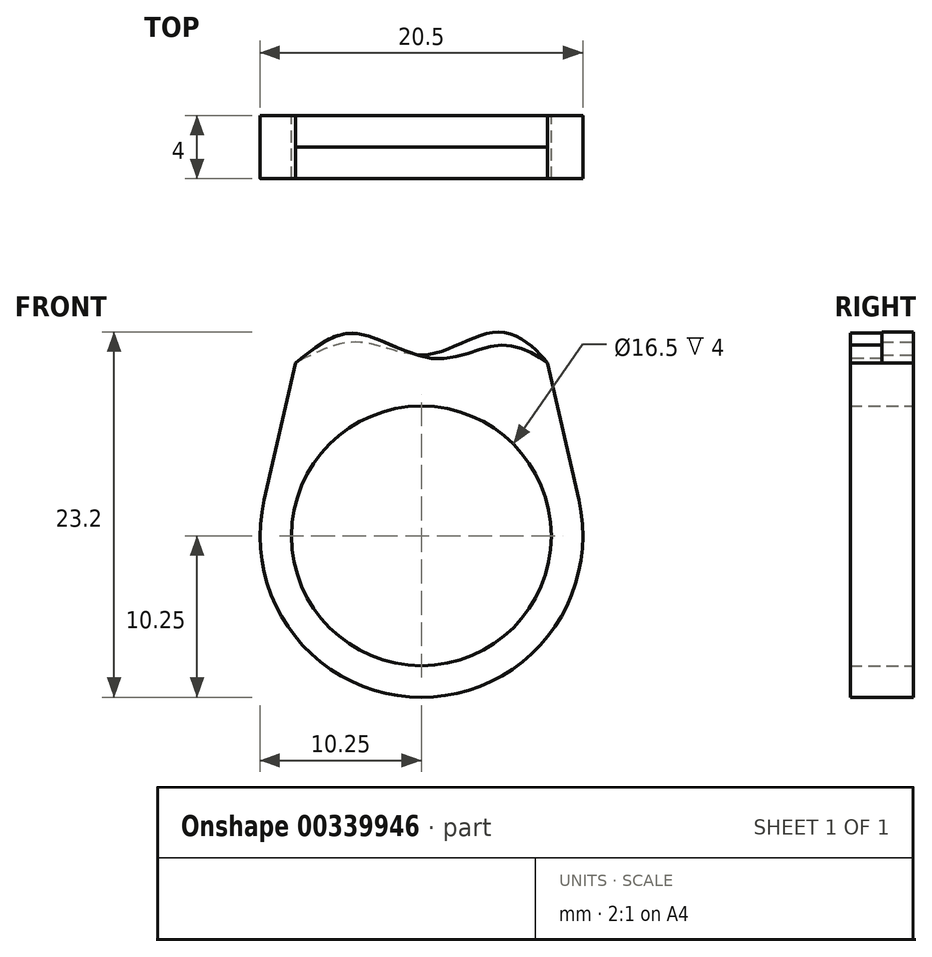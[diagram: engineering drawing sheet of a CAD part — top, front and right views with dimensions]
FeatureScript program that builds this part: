
annotation { "Feature Type Name" : "Feature", "Feature Type Description" : "" }
export const myFeature = defineFeature(function(context is Context, id is Id, definition is map)
    precondition{}
    {
        {
            var Q0;
            Q0=qCreatedBy(makeId("Front.planeOp"),FACE);
            var sketch = newSketch(context, id + "F0", { "sketchPlane" : qUnion([Q0])});
            skCircle(sketch, "E0", {"center": v(0, 0) * mm, "radius": 8.25 * mm});
            skCircle(sketch, "E1", {"center": v(0, 0) * mm, "radius": 10.25 * mm});
            skLineSegment(sketch, "E2", {"start": v(-10, 2.28) * mm, "end": v(-8, 11) * mm});
            skLineSegment(sketch, "E3", {"start": v(-8, 11) * mm, "end": v(8, 11) * mm});
            skLineSegment(sketch, "E4", {"start": v(8, 11) * mm, "end": v(10, 2.28) * mm});
            skLineSegment(sketch, "E5", {"start": v(0, 11) * mm, "end": v(0, 0) * mm});
            skSolve(sketch);
        }
        {
            var Q0;
            Q0 = qSketchRegion(id + "F0", true);
            extrude(context, id + "F1", {"entities" : qUnion([Q0]), "depth" : 2 * mm, "hasSecondDirection" : true, "secondDirectionOppositeDirection" : true, "secondDirectionDepth" : 2 * mm});
        }
        {
            var Q0;
            Q0=makeQuery(id+"F1.opExtrude","CAP_FACE",FACE,{"disambiguationData":[OSD([sQuery(id+"F0.wireOp",EDGE,"E0"),sQuery(id+"F0.wireOp",EDGE,"E1"),sQuery(id+"F0.wireOp",EDGE,"E2"),sQuery(id+"F0.wireOp",EDGE,"E3"),sQuery(id+"F0.wireOp",EDGE,"E4")])],"isStart":false});
            var sketch = newSketch(context, id + "F2", { "sketchPlane" : qUnion([Q0])});
            skFitSpline(sketch, "E6", {"points": [v(-8, 11) * mm, v(-4.31, 12.87) * mm, v(0.78, 11.26) * mm, v(5.12, 12.12) * mm, v(8, 11) * mm], "startDerivative": vector(15.2, 11.43) * mm, "endDerivative": vector(10.8, -7.66) * mm});
            skLineSegment(sketch, "E7", {"start": v(-8, 11) * mm, "end": v(8, 11) * mm});
            skSolve(sketch);
        }
        {
            var Q0;
            Q0 = qSketchRegion(id + "F2", true);
            extrude(context, id + "F3", {"entities" : qUnion([Q0]), "operationType" : NewBodyOperationType.ADD, "oppositeDirection" : true, "depth" : 2 * mm});
        }
        {
            var Q0;
            Q0=makeQuery(id+"F1.opExtrude","CAP_FACE",FACE,{"disambiguationData":[OSD([sQuery(id+"F0.wireOp",EDGE,"E0"),sQuery(id+"F0.wireOp",EDGE,"E1"),sQuery(id+"F0.wireOp",EDGE,"E2"),sQuery(id+"F0.wireOp",EDGE,"E3"),sQuery(id+"F0.wireOp",EDGE,"E4")])],"isStart":true});
            var sketch = newSketch(context, id + "F4", { "sketchPlane" : qUnion([Q0])});
            skFitSpline(sketch, "E8", {"points": [v(-8, 11) * mm, v(-4.96, 12.95) * mm, v(-0.34, 11.51) * mm, v(4.16, 12.31) * mm, v(8, 11) * mm], "startDerivative": vector(8.84, 10.98) * mm, "endDerivative": vector(14.38, -6.84) * mm});
            skLineSegment(sketch, "E9", {"start": v(-8, 11) * mm, "end": v(8, 11) * mm});
            skSolve(sketch);
        }
        {
            var Q0;
            Q0 = qSketchRegion(id + "F4", true);
            extrude(context, id + "F5", {"entities" : qUnion([Q0]), "operationType" : NewBodyOperationType.ADD, "oppositeDirection" : true, "depth" : 2 * mm});
        }
    });
